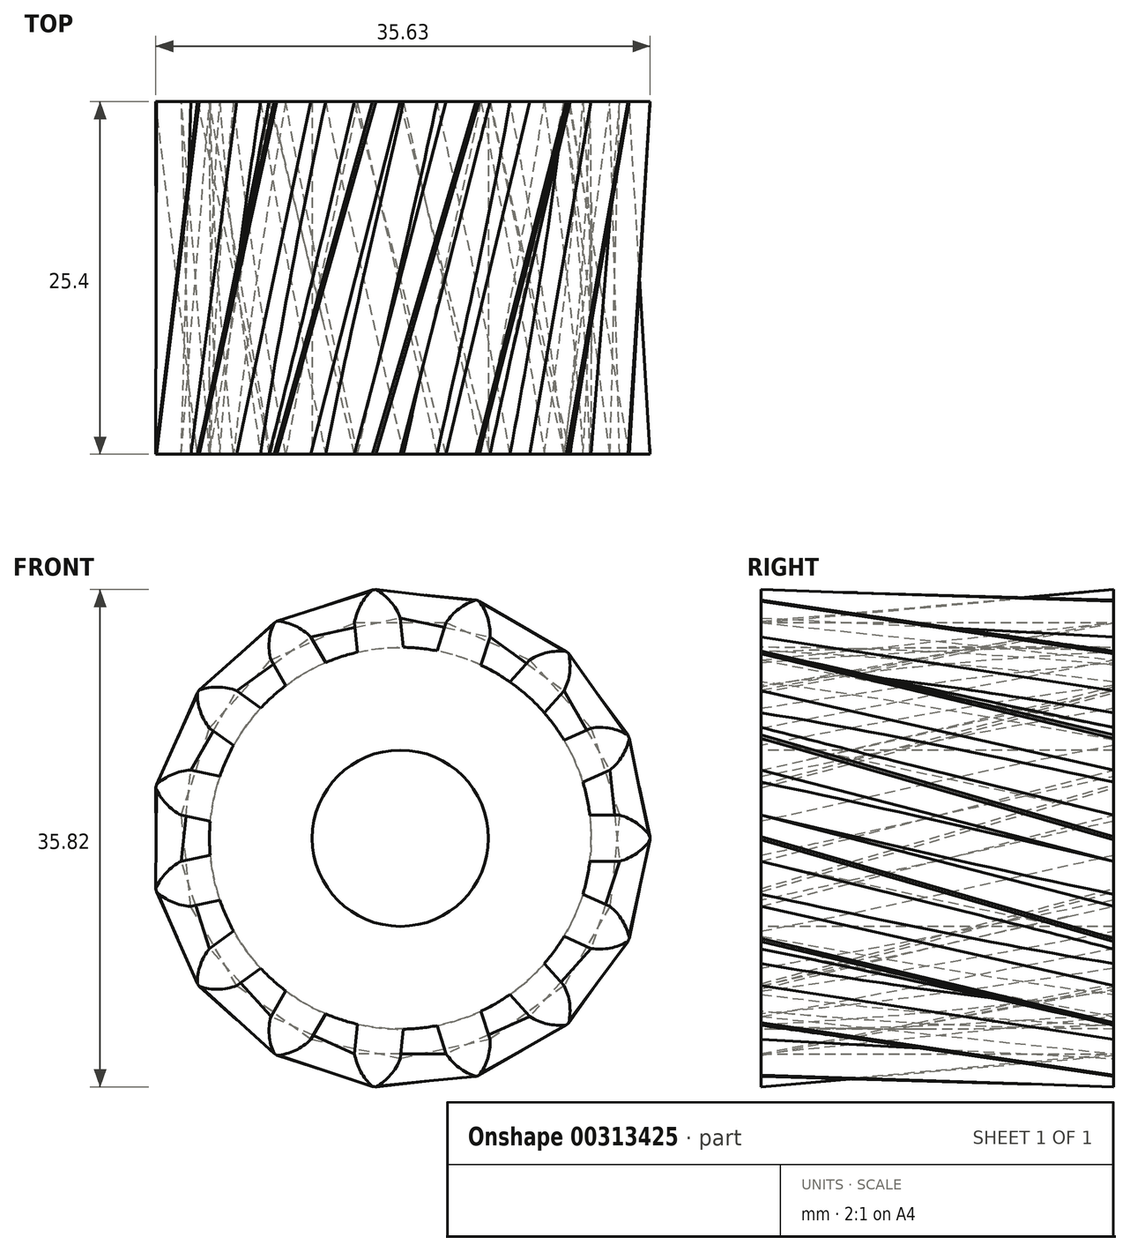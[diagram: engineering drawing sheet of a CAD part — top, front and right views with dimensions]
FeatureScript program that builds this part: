
annotation { "Feature Type Name" : "Feature", "Feature Type Description" : "" }
export const myFeature = defineFeature(function(context is Context, id is Id, definition is map)
    precondition{}
    {
        {
            var Q0;
            Q0=qCreatedBy(makeId("Front.planeOp"),FACE);
            var sketch = newSketch(context, id + "F0", { "sketchPlane" : qUnion([Q0])});
            skCircle(sketch, "E0", {"center": v(0, 0) * mm, "radius": 13.75 * mm});
            skArc(sketch, "E1.trimOffspring", {"start": v(0, 15.88) * mm, "mid": v(-0.7, 17.05) * mm, "end": v(-1.76, 17.9) * mm});
            skLineSegment(sketch, "E2", {"start": v(0, 15.88) * mm, "end": v(0.22, 13.75) * mm});
            skLineSegment(sketch, "E3", {"start": v(-1.76, 17.9) * mm, "end": v(-1.88, 17.9) * mm});
            skLineSegment(sketch, "E4.MirrorCS", {"start": v(-3.3, 15.53) * mm, "end": v(-3.08, 13.4) * mm});
            skArc(sketch, "E5.MirrorCS", {"start": v(-3.3, 15.53) * mm, "mid": v(-2.86, 16.82) * mm, "end": v(-2, 17.88) * mm});
            skLineSegment(sketch, "E6.MirrorCS", {"start": v(-2, 17.88) * mm, "end": v(-1.88, 17.9) * mm});
            skLineSegment(sketch, "E7.1.0", {"start": v(-6.46, 14.5) * mm, "end": v(-5.39, 12.65) * mm});
            skArc(sketch, "E7.1.1", {"start": v(-6.46, 14.5) * mm, "mid": v(-7.57, 15.29) * mm, "end": v(-8.9, 15.65) * mm});
            skLineSegment(sketch, "E7.1.2", {"start": v(-8.9, 15.65) * mm, "end": v(-9, 15.59) * mm});
            skLineSegment(sketch, "E7.1.3", {"start": v(-9.1, 15.52) * mm, "end": v(-9, 15.59) * mm});
            skArc(sketch, "E7.1.4", {"start": v(-9.33, 12.84) * mm, "mid": v(-9.45, 14.2) * mm, "end": v(-9.1, 15.52) * mm});
            skLineSegment(sketch, "E7.1.5", {"start": v(-9.33, 12.84) * mm, "end": v(-8.26, 11) * mm});
            skLineSegment(sketch, "E7.2.0", {"start": v(-11.8, 10.62) * mm, "end": v(-10.07, 9.37) * mm});
            skArc(sketch, "E7.2.1", {"start": v(-11.8, 10.62) * mm, "mid": v(-13.14, 10.88) * mm, "end": v(-14.49, 10.68) * mm});
            skLineSegment(sketch, "E7.2.2", {"start": v(-14.49, 10.68) * mm, "end": v(-14.56, 10.58) * mm});
            skLineSegment(sketch, "E7.2.3", {"start": v(-14.63, 10.48) * mm, "end": v(-14.56, 10.58) * mm});
            skArc(sketch, "E7.2.4", {"start": v(-13.75, 7.94) * mm, "mid": v(-14.41, 9.13) * mm, "end": v(-14.63, 10.48) * mm});
            skLineSegment(sketch, "E7.2.5", {"start": v(-13.75, 7.94) * mm, "end": v(-12.02, 6.68) * mm});
            skLineSegment(sketch, "E7.3.0", {"start": v(-15.1, 4.9) * mm, "end": v(-13.01, 4.46) * mm});
            skArc(sketch, "E7.3.1", {"start": v(-15.1, 4.9) * mm, "mid": v(-16.43, 4.6) * mm, "end": v(-17.58, 3.86) * mm});
            skLineSegment(sketch, "E7.3.2", {"start": v(-17.58, 3.86) * mm, "end": v(-17.6, 3.74) * mm});
            skLineSegment(sketch, "E7.3.3", {"start": v(-17.63, 3.62) * mm, "end": v(-17.6, 3.74) * mm});
            skArc(sketch, "E7.3.4", {"start": v(-15.79, 1.66) * mm, "mid": v(-16.88, 2.48) * mm, "end": v(-17.63, 3.62) * mm});
            skLineSegment(sketch, "E7.3.5", {"start": v(-15.79, 1.66) * mm, "end": v(-13.7, 1.22) * mm});
            skLineSegment(sketch, "E7.4.0", {"start": v(-15.79, -1.66) * mm, "end": v(-13.7, -1.22) * mm});
            skArc(sketch, "E7.4.1", {"start": v(-15.79, -1.66) * mm, "mid": v(-16.88, -2.48) * mm, "end": v(-17.63, -3.62) * mm});
            skLineSegment(sketch, "E7.4.2", {"start": v(-17.63, -3.62) * mm, "end": v(-17.6, -3.74) * mm});
            skLineSegment(sketch, "E7.4.3", {"start": v(-17.58, -3.86) * mm, "end": v(-17.6, -3.74) * mm});
            skArc(sketch, "E7.4.4", {"start": v(-15.1, -4.9) * mm, "mid": v(-16.43, -4.6) * mm, "end": v(-17.58, -3.86) * mm});
            skLineSegment(sketch, "E7.4.5", {"start": v(-15.1, -4.9) * mm, "end": v(-13.01, -4.46) * mm});
            skLineSegment(sketch, "E7.5.0", {"start": v(-13.75, -7.94) * mm, "end": v(-12.02, -6.68) * mm});
            skArc(sketch, "E7.5.1", {"start": v(-13.75, -7.94) * mm, "mid": v(-14.41, -9.13) * mm, "end": v(-14.63, -10.48) * mm});
            skLineSegment(sketch, "E7.5.2", {"start": v(-14.63, -10.48) * mm, "end": v(-14.56, -10.58) * mm});
            skLineSegment(sketch, "E7.5.3", {"start": v(-14.49, -10.68) * mm, "end": v(-14.56, -10.58) * mm});
            skArc(sketch, "E7.5.4", {"start": v(-11.8, -10.62) * mm, "mid": v(-13.14, -10.88) * mm, "end": v(-14.49, -10.68) * mm});
            skLineSegment(sketch, "E7.5.5", {"start": v(-11.8, -10.62) * mm, "end": v(-10.07, -9.37) * mm});
            skLineSegment(sketch, "E7.6.0", {"start": v(-9.33, -12.84) * mm, "end": v(-8.26, -11) * mm});
            skArc(sketch, "E7.6.1", {"start": v(-9.33, -12.84) * mm, "mid": v(-9.45, -14.2) * mm, "end": v(-9.1, -15.52) * mm});
            skLineSegment(sketch, "E7.6.2", {"start": v(-9.1, -15.52) * mm, "end": v(-9, -15.59) * mm});
            skLineSegment(sketch, "E7.6.3", {"start": v(-8.9, -15.65) * mm, "end": v(-9, -15.59) * mm});
            skArc(sketch, "E7.6.4", {"start": v(-6.46, -14.5) * mm, "mid": v(-7.57, -15.29) * mm, "end": v(-8.9, -15.65) * mm});
            skLineSegment(sketch, "E7.6.5", {"start": v(-6.46, -14.5) * mm, "end": v(-5.39, -12.65) * mm});
            skLineSegment(sketch, "E7.7.0", {"start": v(-3.3, -15.53) * mm, "end": v(-3.08, -13.4) * mm});
            skArc(sketch, "E7.7.1", {"start": v(-3.3, -15.53) * mm, "mid": v(-2.86, -16.82) * mm, "end": v(-2, -17.88) * mm});
            skLineSegment(sketch, "E7.7.2", {"start": v(-2, -17.88) * mm, "end": v(-1.88, -17.9) * mm});
            skLineSegment(sketch, "E7.7.3", {"start": v(-1.76, -17.9) * mm, "end": v(-1.88, -17.9) * mm});
            skArc(sketch, "E7.7.4", {"start": v(0, -15.88) * mm, "mid": v(-0.7, -17.05) * mm, "end": v(-1.76, -17.9) * mm});
            skLineSegment(sketch, "E7.7.5", {"start": v(0, -15.88) * mm, "end": v(0.22, -13.75) * mm});
            skLineSegment(sketch, "E7.8.0", {"start": v(3.3, -15.53) * mm, "end": v(2.64, -13.5) * mm});
            skArc(sketch, "E7.8.1", {"start": v(3.3, -15.53) * mm, "mid": v(4.23, -16.53) * mm, "end": v(5.44, -17.15) * mm});
            skLineSegment(sketch, "E7.8.2", {"start": v(5.44, -17.15) * mm, "end": v(5.56, -17.12) * mm});
            skLineSegment(sketch, "E7.8.3", {"start": v(5.68, -17.08) * mm, "end": v(5.56, -17.12) * mm});
            skArc(sketch, "E7.8.4", {"start": v(6.46, -14.5) * mm, "mid": v(6.3, -15.86) * mm, "end": v(5.68, -17.08) * mm});
            skLineSegment(sketch, "E7.8.5", {"start": v(6.46, -14.5) * mm, "end": v(5.8, -12.47) * mm});
            skLineSegment(sketch, "E7.9.0", {"start": v(9.33, -12.84) * mm, "end": v(7.9, -11.26) * mm});
            skArc(sketch, "E7.9.1", {"start": v(9.33, -12.84) * mm, "mid": v(10.59, -13.38) * mm, "end": v(11.95, -13.46) * mm});
            skLineSegment(sketch, "E7.9.2", {"start": v(11.95, -13.46) * mm, "end": v(12.04, -13.37) * mm});
            skLineSegment(sketch, "E7.9.3", {"start": v(12.13, -13.3) * mm, "end": v(12.04, -13.37) * mm});
            skArc(sketch, "E7.9.4", {"start": v(11.8, -10.62) * mm, "mid": v(12.2, -11.93) * mm, "end": v(12.13, -13.3) * mm});
            skLineSegment(sketch, "E7.9.5", {"start": v(11.8, -10.62) * mm, "end": v(10.37, -9.04) * mm});
            skLineSegment(sketch, "E7.10.0", {"start": v(13.75, -7.94) * mm, "end": v(11.8, -7.07) * mm});
            skArc(sketch, "E7.10.1", {"start": v(13.75, -7.94) * mm, "mid": v(15.11, -7.92) * mm, "end": v(16.39, -7.43) * mm});
            skLineSegment(sketch, "E7.10.2", {"start": v(16.39, -7.43) * mm, "end": v(16.44, -7.32) * mm});
            skLineSegment(sketch, "E7.10.3", {"start": v(16.49, -7.2) * mm, "end": v(16.44, -7.32) * mm});
            skArc(sketch, "E7.10.4", {"start": v(15.1, -4.9) * mm, "mid": v(16, -5.94) * mm, "end": v(16.49, -7.2) * mm});
            skLineSegment(sketch, "E7.10.5", {"start": v(15.1, -4.9) * mm, "end": v(13.15, -4.04) * mm});
            skLineSegment(sketch, "E7.11.0", {"start": v(15.79, -1.66) * mm, "end": v(13.65, -1.66) * mm});
            skArc(sketch, "E7.11.1", {"start": v(15.79, -1.66) * mm, "mid": v(17.03, -1.08) * mm, "end": v(18, -0.12) * mm});
            skLineSegment(sketch, "E7.11.2", {"start": v(18, -0.12) * mm, "end": v(18, 0) * mm});
            skLineSegment(sketch, "E7.11.3", {"start": v(18, 0.12) * mm, "end": v(18, 0) * mm});
            skArc(sketch, "E7.11.4", {"start": v(15.79, 1.66) * mm, "mid": v(17.03, 1.08) * mm, "end": v(18, 0.12) * mm});
            skLineSegment(sketch, "E7.11.5", {"start": v(15.79, 1.66) * mm, "end": v(13.65, 1.66) * mm});
            skLineSegment(sketch, "E7.12.0", {"start": v(15.1, 4.9) * mm, "end": v(13.15, 4.04) * mm});
            skArc(sketch, "E7.12.1", {"start": v(15.1, 4.9) * mm, "mid": v(16, 5.94) * mm, "end": v(16.49, 7.2) * mm});
            skLineSegment(sketch, "E7.12.2", {"start": v(16.49, 7.2) * mm, "end": v(16.44, 7.32) * mm});
            skLineSegment(sketch, "E7.12.3", {"start": v(16.39, 7.43) * mm, "end": v(16.44, 7.32) * mm});
            skArc(sketch, "E7.12.4", {"start": v(13.75, 7.94) * mm, "mid": v(15.11, 7.92) * mm, "end": v(16.39, 7.43) * mm});
            skLineSegment(sketch, "E7.12.5", {"start": v(13.75, 7.94) * mm, "end": v(11.8, 7.07) * mm});
            skLineSegment(sketch, "E7.13.0", {"start": v(11.8, 10.62) * mm, "end": v(10.37, 9.04) * mm});
            skArc(sketch, "E7.13.1", {"start": v(11.8, 10.62) * mm, "mid": v(12.2, 11.93) * mm, "end": v(12.13, 13.3) * mm});
            skLineSegment(sketch, "E7.13.2", {"start": v(12.13, 13.3) * mm, "end": v(12.04, 13.37) * mm});
            skLineSegment(sketch, "E7.13.3", {"start": v(11.95, 13.46) * mm, "end": v(12.04, 13.37) * mm});
            skArc(sketch, "E7.13.4", {"start": v(9.33, 12.84) * mm, "mid": v(10.59, 13.38) * mm, "end": v(11.95, 13.46) * mm});
            skLineSegment(sketch, "E7.13.5", {"start": v(9.33, 12.84) * mm, "end": v(7.9, 11.26) * mm});
            skLineSegment(sketch, "E7.14.0", {"start": v(6.46, 14.5) * mm, "end": v(5.8, 12.47) * mm});
            skArc(sketch, "E7.14.1", {"start": v(6.46, 14.5) * mm, "mid": v(6.3, 15.86) * mm, "end": v(5.68, 17.08) * mm});
            skLineSegment(sketch, "E7.14.2", {"start": v(5.68, 17.08) * mm, "end": v(5.56, 17.12) * mm});
            skLineSegment(sketch, "E7.14.3", {"start": v(5.44, 17.15) * mm, "end": v(5.56, 17.12) * mm});
            skArc(sketch, "E7.14.4", {"start": v(3.3, 15.53) * mm, "mid": v(4.23, 16.53) * mm, "end": v(5.44, 17.15) * mm});
            skLineSegment(sketch, "E7.14.5", {"start": v(3.3, 15.53) * mm, "end": v(2.64, 13.5) * mm});
            skSolve(sketch);
        }
        {
            var Q0;
            Q0=qCreatedBy(makeId("Front.planeOp"),FACE);
            cPlane(context, id + "F1", {"entities" : qUnion([Q0]), "cplaneType" : CPlaneType.OFFSET, "offset" : 25.4 * mm, "width" : 152.4 * mm, "height" : 152.4 * mm});
        }
        {
            var Q0;
            Q0=qCreatedBy(id+"F1.planeOp",FACE);
            var sketch = newSketch(context, id + "F2", { "sketchPlane" : qUnion([Q0])});
            skCircle(sketch, "E8", {"center": v(0, 0) * mm, "radius": 13.75 * mm});
            skArc(sketch, "E9.trimOffspring", {"start": v(0, 15.88) * mm, "mid": v(-0.7, 17.05) * mm, "end": v(-1.76, 17.9) * mm});
            skLineSegment(sketch, "E10", {"start": v(0, 15.88) * mm, "end": v(0.22, 13.75) * mm});
            skLineSegment(sketch, "E11", {"start": v(-1.76, 17.9) * mm, "end": v(-1.88, 17.9) * mm});
            skLineSegment(sketch, "E12.MirrorCS", {"start": v(-3.3, 15.53) * mm, "end": v(-3.08, 13.4) * mm});
            skArc(sketch, "E13.MirrorCS", {"start": v(-3.3, 15.53) * mm, "mid": v(-2.86, 16.82) * mm, "end": v(-2, 17.88) * mm});
            skLineSegment(sketch, "E14.MirrorCS", {"start": v(-2, 17.88) * mm, "end": v(-1.88, 17.9) * mm});
            skLineSegment(sketch, "E15.1.0", {"start": v(-6.46, 14.5) * mm, "end": v(-5.39, 12.65) * mm});
            skArc(sketch, "E15.1.1", {"start": v(-6.46, 14.5) * mm, "mid": v(-7.57, 15.29) * mm, "end": v(-8.9, 15.65) * mm});
            skLineSegment(sketch, "E15.1.2", {"start": v(-8.9, 15.65) * mm, "end": v(-9, 15.59) * mm});
            skLineSegment(sketch, "E15.1.3", {"start": v(-9.1, 15.52) * mm, "end": v(-9, 15.59) * mm});
            skArc(sketch, "E15.1.4", {"start": v(-9.33, 12.84) * mm, "mid": v(-9.45, 14.2) * mm, "end": v(-9.1, 15.52) * mm});
            skLineSegment(sketch, "E15.1.5", {"start": v(-9.33, 12.84) * mm, "end": v(-8.26, 11) * mm});
            skLineSegment(sketch, "E15.2.0", {"start": v(-11.8, 10.62) * mm, "end": v(-10.07, 9.37) * mm});
            skArc(sketch, "E15.2.1", {"start": v(-11.8, 10.62) * mm, "mid": v(-13.14, 10.88) * mm, "end": v(-14.49, 10.68) * mm});
            skLineSegment(sketch, "E15.2.2", {"start": v(-14.49, 10.68) * mm, "end": v(-14.56, 10.58) * mm});
            skLineSegment(sketch, "E15.2.3", {"start": v(-14.63, 10.48) * mm, "end": v(-14.56, 10.58) * mm});
            skArc(sketch, "E15.2.4", {"start": v(-13.75, 7.94) * mm, "mid": v(-14.41, 9.13) * mm, "end": v(-14.63, 10.48) * mm});
            skLineSegment(sketch, "E15.2.5", {"start": v(-13.75, 7.94) * mm, "end": v(-12.02, 6.68) * mm});
            skLineSegment(sketch, "E15.3.0", {"start": v(-15.1, 4.9) * mm, "end": v(-13.01, 4.46) * mm});
            skArc(sketch, "E15.3.1", {"start": v(-15.1, 4.9) * mm, "mid": v(-16.43, 4.6) * mm, "end": v(-17.58, 3.86) * mm});
            skLineSegment(sketch, "E15.3.2", {"start": v(-17.58, 3.86) * mm, "end": v(-17.6, 3.74) * mm});
            skLineSegment(sketch, "E15.3.3", {"start": v(-17.63, 3.62) * mm, "end": v(-17.6, 3.74) * mm});
            skArc(sketch, "E15.3.4", {"start": v(-15.79, 1.66) * mm, "mid": v(-16.88, 2.48) * mm, "end": v(-17.63, 3.62) * mm});
            skLineSegment(sketch, "E15.3.5", {"start": v(-15.79, 1.66) * mm, "end": v(-13.7, 1.22) * mm});
            skLineSegment(sketch, "E15.4.0", {"start": v(-15.79, -1.66) * mm, "end": v(-13.7, -1.22) * mm});
            skArc(sketch, "E15.4.1", {"start": v(-15.79, -1.66) * mm, "mid": v(-16.88, -2.48) * mm, "end": v(-17.63, -3.62) * mm});
            skLineSegment(sketch, "E15.4.2", {"start": v(-17.63, -3.62) * mm, "end": v(-17.6, -3.74) * mm});
            skLineSegment(sketch, "E15.4.3", {"start": v(-17.58, -3.86) * mm, "end": v(-17.6, -3.74) * mm});
            skArc(sketch, "E15.4.4", {"start": v(-15.1, -4.9) * mm, "mid": v(-16.43, -4.6) * mm, "end": v(-17.58, -3.86) * mm});
            skLineSegment(sketch, "E15.4.5", {"start": v(-15.1, -4.9) * mm, "end": v(-13.01, -4.46) * mm});
            skLineSegment(sketch, "E15.5.0", {"start": v(-13.75, -7.94) * mm, "end": v(-12.02, -6.68) * mm});
            skArc(sketch, "E15.5.1", {"start": v(-13.75, -7.94) * mm, "mid": v(-14.41, -9.13) * mm, "end": v(-14.63, -10.48) * mm});
            skLineSegment(sketch, "E15.5.2", {"start": v(-14.63, -10.48) * mm, "end": v(-14.56, -10.58) * mm});
            skLineSegment(sketch, "E15.5.3", {"start": v(-14.49, -10.68) * mm, "end": v(-14.56, -10.58) * mm});
            skArc(sketch, "E15.5.4", {"start": v(-11.8, -10.62) * mm, "mid": v(-13.14, -10.88) * mm, "end": v(-14.49, -10.68) * mm});
            skLineSegment(sketch, "E15.5.5", {"start": v(-11.8, -10.62) * mm, "end": v(-10.07, -9.37) * mm});
            skLineSegment(sketch, "E15.6.0", {"start": v(-9.33, -12.84) * mm, "end": v(-8.26, -11) * mm});
            skArc(sketch, "E15.6.1", {"start": v(-9.33, -12.84) * mm, "mid": v(-9.45, -14.2) * mm, "end": v(-9.1, -15.52) * mm});
            skLineSegment(sketch, "E15.6.2", {"start": v(-9.1, -15.52) * mm, "end": v(-9, -15.59) * mm});
            skLineSegment(sketch, "E15.6.3", {"start": v(-8.9, -15.65) * mm, "end": v(-9, -15.59) * mm});
            skArc(sketch, "E15.6.4", {"start": v(-6.46, -14.5) * mm, "mid": v(-7.57, -15.29) * mm, "end": v(-8.9, -15.65) * mm});
            skLineSegment(sketch, "E15.6.5", {"start": v(-6.46, -14.5) * mm, "end": v(-5.39, -12.65) * mm});
            skLineSegment(sketch, "E15.7.0", {"start": v(-3.3, -15.53) * mm, "end": v(-3.08, -13.4) * mm});
            skArc(sketch, "E15.7.1", {"start": v(-3.3, -15.53) * mm, "mid": v(-2.86, -16.82) * mm, "end": v(-2, -17.88) * mm});
            skLineSegment(sketch, "E15.7.2", {"start": v(-2, -17.88) * mm, "end": v(-1.88, -17.9) * mm});
            skLineSegment(sketch, "E15.7.3", {"start": v(-1.76, -17.9) * mm, "end": v(-1.88, -17.9) * mm});
            skArc(sketch, "E15.7.4", {"start": v(0, -15.88) * mm, "mid": v(-0.7, -17.05) * mm, "end": v(-1.76, -17.9) * mm});
            skLineSegment(sketch, "E15.7.5", {"start": v(0, -15.88) * mm, "end": v(0.22, -13.75) * mm});
            skLineSegment(sketch, "E15.8.0", {"start": v(3.3, -15.53) * mm, "end": v(2.64, -13.5) * mm});
            skArc(sketch, "E15.8.1", {"start": v(3.3, -15.53) * mm, "mid": v(4.23, -16.53) * mm, "end": v(5.44, -17.15) * mm});
            skLineSegment(sketch, "E15.8.2", {"start": v(5.44, -17.15) * mm, "end": v(5.56, -17.12) * mm});
            skLineSegment(sketch, "E15.8.3", {"start": v(5.68, -17.08) * mm, "end": v(5.56, -17.12) * mm});
            skArc(sketch, "E15.8.4", {"start": v(6.46, -14.5) * mm, "mid": v(6.3, -15.86) * mm, "end": v(5.68, -17.08) * mm});
            skLineSegment(sketch, "E15.8.5", {"start": v(6.46, -14.5) * mm, "end": v(5.8, -12.47) * mm});
            skLineSegment(sketch, "E15.9.0", {"start": v(9.33, -12.84) * mm, "end": v(7.9, -11.26) * mm});
            skArc(sketch, "E15.9.1", {"start": v(9.33, -12.84) * mm, "mid": v(10.59, -13.38) * mm, "end": v(11.95, -13.46) * mm});
            skLineSegment(sketch, "E15.9.2", {"start": v(11.95, -13.46) * mm, "end": v(12.04, -13.37) * mm});
            skLineSegment(sketch, "E15.9.3", {"start": v(12.13, -13.3) * mm, "end": v(12.04, -13.37) * mm});
            skArc(sketch, "E15.9.4", {"start": v(11.8, -10.62) * mm, "mid": v(12.2, -11.93) * mm, "end": v(12.13, -13.3) * mm});
            skLineSegment(sketch, "E15.9.5", {"start": v(11.8, -10.62) * mm, "end": v(10.37, -9.04) * mm});
            skLineSegment(sketch, "E15.10.0", {"start": v(13.75, -7.94) * mm, "end": v(11.8, -7.07) * mm});
            skArc(sketch, "E15.10.1", {"start": v(13.75, -7.94) * mm, "mid": v(15.11, -7.92) * mm, "end": v(16.39, -7.43) * mm});
            skLineSegment(sketch, "E15.10.2", {"start": v(16.39, -7.43) * mm, "end": v(16.44, -7.32) * mm});
            skLineSegment(sketch, "E15.10.3", {"start": v(16.49, -7.2) * mm, "end": v(16.44, -7.32) * mm});
            skArc(sketch, "E15.10.4", {"start": v(15.1, -4.9) * mm, "mid": v(16, -5.94) * mm, "end": v(16.49, -7.2) * mm});
            skLineSegment(sketch, "E15.10.5", {"start": v(15.1, -4.9) * mm, "end": v(13.15, -4.04) * mm});
            skLineSegment(sketch, "E15.11.0", {"start": v(15.79, -1.66) * mm, "end": v(13.65, -1.66) * mm});
            skArc(sketch, "E15.11.1", {"start": v(15.79, -1.66) * mm, "mid": v(17.03, -1.08) * mm, "end": v(18, -0.12) * mm});
            skLineSegment(sketch, "E15.11.2", {"start": v(18, -0.12) * mm, "end": v(18, 0) * mm});
            skLineSegment(sketch, "E15.11.3", {"start": v(18, 0.12) * mm, "end": v(18, 0) * mm});
            skArc(sketch, "E15.11.4", {"start": v(15.79, 1.66) * mm, "mid": v(17.03, 1.08) * mm, "end": v(18, 0.12) * mm});
            skLineSegment(sketch, "E15.11.5", {"start": v(15.79, 1.66) * mm, "end": v(13.65, 1.66) * mm});
            skLineSegment(sketch, "E15.12.0", {"start": v(15.1, 4.9) * mm, "end": v(13.15, 4.04) * mm});
            skArc(sketch, "E15.12.1", {"start": v(15.1, 4.9) * mm, "mid": v(16, 5.94) * mm, "end": v(16.49, 7.2) * mm});
            skLineSegment(sketch, "E15.12.2", {"start": v(16.49, 7.2) * mm, "end": v(16.44, 7.32) * mm});
            skLineSegment(sketch, "E15.12.3", {"start": v(16.39, 7.43) * mm, "end": v(16.44, 7.32) * mm});
            skArc(sketch, "E15.12.4", {"start": v(13.75, 7.94) * mm, "mid": v(15.11, 7.92) * mm, "end": v(16.39, 7.43) * mm});
            skLineSegment(sketch, "E15.12.5", {"start": v(13.75, 7.94) * mm, "end": v(11.8, 7.07) * mm});
            skLineSegment(sketch, "E15.13.0", {"start": v(11.8, 10.62) * mm, "end": v(10.37, 9.04) * mm});
            skArc(sketch, "E15.13.1", {"start": v(11.8, 10.62) * mm, "mid": v(12.2, 11.93) * mm, "end": v(12.13, 13.3) * mm});
            skLineSegment(sketch, "E15.13.2", {"start": v(12.13, 13.3) * mm, "end": v(12.04, 13.37) * mm});
            skLineSegment(sketch, "E15.13.3", {"start": v(11.95, 13.46) * mm, "end": v(12.04, 13.37) * mm});
            skArc(sketch, "E15.13.4", {"start": v(9.33, 12.84) * mm, "mid": v(10.59, 13.38) * mm, "end": v(11.95, 13.46) * mm});
            skLineSegment(sketch, "E15.13.5", {"start": v(9.33, 12.84) * mm, "end": v(7.9, 11.26) * mm});
            skLineSegment(sketch, "E15.14.0", {"start": v(6.46, 14.5) * mm, "end": v(5.8, 12.47) * mm});
            skArc(sketch, "E15.14.1", {"start": v(6.46, 14.5) * mm, "mid": v(6.3, 15.86) * mm, "end": v(5.68, 17.08) * mm});
            skLineSegment(sketch, "E15.14.2", {"start": v(5.68, 17.08) * mm, "end": v(5.56, 17.12) * mm});
            skLineSegment(sketch, "E15.14.3", {"start": v(5.44, 17.15) * mm, "end": v(5.56, 17.12) * mm});
            skArc(sketch, "E15.14.4", {"start": v(3.3, 15.53) * mm, "mid": v(4.23, 16.53) * mm, "end": v(5.44, 17.15) * mm});
            skLineSegment(sketch, "E15.14.5", {"start": v(3.3, 15.53) * mm, "end": v(2.64, 13.5) * mm});
            skSolve(sketch);
        }
        {
            var Q0;
            Q0=makeQuery(id+"F2.imprint","IMPRINT",FACE,{"disambiguationData":[TD([[makeQuery(id+"F2.imprint","IMPRINT",EDGE,{"derivedFrom":sQuery(id+"F2.wireOp",EDGE,"E9.trimOffspring")}),1.0]])]});
            var Q1;
            {var subQ0=sQuery(id+"F0.wireOp",EDGE,"E7.14.0");Q1=makeQuery(id+"F0.imprint","IMPRINT",FACE,{"disambiguationData":[TD([[makeQuery(id+"F0.imprint","IMPRINT",EDGE,{"derivedFrom":subQ0}),-1.0]])]});}
            loft(context, id + "F3", {"sheetProfilesArray" : [{ "sheetProfileEntities" : qUnion([Q0]) }, { "sheetProfileEntities" : qUnion([Q1]) }]});
        }
        {
            var Q1;
            {var subQ0=sQuery(id+"F2.wireOp",EDGE,"E8");var subQ18=makeQuery(id+"F2.imprint","INTERSECT",VERTEX,{"derivedFrom":[subQ0,sQuery(id+"F2.wireOp",EDGE,"E15.11.5")]});Q1=makeQuery(id+"F2.imprint","IMPRINT",FACE,{"disambiguationData":[TD([[makeQuery(id+"F2.imprint","IMPRINT",EDGE,{"disambiguationData":[TD([[subQ18,-1.0]])],"derivedFrom":subQ0}),1.0]])]});}
            var Q2;
            {var subQ0=sQuery(id+"F0.wireOp",EDGE,"E0");var subQ18=makeQuery(id+"F0.imprint","INTERSECT",VERTEX,{"derivedFrom":[subQ0,sQuery(id+"F0.wireOp",EDGE,"E7.11.5")]});Q2=makeQuery(id+"F0.imprint","IMPRINT",FACE,{"disambiguationData":[TD([[makeQuery(id+"F0.imprint","IMPRINT",EDGE,{"disambiguationData":[TD([[subQ18,-1.0]])],"derivedFrom":subQ0}),1.0]])]});}
            loft(context, id + "F4", {"operationType" : NewBodyOperationType.ADD, "sheetProfilesArray" : [{ "sheetProfileEntities" : qUnion([Q1]) }, { "sheetProfileEntities" : qUnion([Q2]) }]});
        }
        {
            var Q1;
            {var subQ0=sQuery(id+"F2.wireOp",EDGE,"E15.14.0");Q1=makeQuery(id+"F2.imprint","IMPRINT",FACE,{"disambiguationData":[TD([[makeQuery(id+"F2.imprint","IMPRINT",EDGE,{"derivedFrom":subQ0}),-1.0]])]});}
            var Q2;
            {var subQ0=sQuery(id+"F0.wireOp",EDGE,"E7.13.0");Q2=makeQuery(id+"F0.imprint","IMPRINT",FACE,{"disambiguationData":[TD([[makeQuery(id+"F0.imprint","IMPRINT",EDGE,{"derivedFrom":subQ0}),-1.0]])]});}
            loft(context, id + "F5", {"operationType" : NewBodyOperationType.ADD, "sheetProfilesArray" : [{ "sheetProfileEntities" : qUnion([Q1]) }, { "sheetProfileEntities" : qUnion([Q2]) }]});
        }
        {
            var Q1;
            {var subQ0=sQuery(id+"F2.wireOp",EDGE,"E15.1.0");Q1=makeQuery(id+"F2.imprint","IMPRINT",FACE,{"disambiguationData":[TD([[makeQuery(id+"F2.imprint","IMPRINT",EDGE,{"derivedFrom":subQ0}),-1.0]])]});}
            var Q2;
            Q2=makeQuery(id+"F0.imprint","IMPRINT",FACE,{"disambiguationData":[TD([[makeQuery(id+"F0.imprint","IMPRINT",EDGE,{"derivedFrom":sQuery(id+"F0.wireOp",EDGE,"E1.trimOffspring")}),1.0]])]});
            loft(context, id + "F6", {"operationType" : NewBodyOperationType.ADD, "sheetProfilesArray" : [{ "sheetProfileEntities" : qUnion([Q1]) }, { "sheetProfileEntities" : qUnion([Q2]) }]});
        }
        {
            var Q1;
            {var subQ0=sQuery(id+"F2.wireOp",EDGE,"E15.2.0");Q1=makeQuery(id+"F2.imprint","IMPRINT",FACE,{"disambiguationData":[TD([[makeQuery(id+"F2.imprint","IMPRINT",EDGE,{"derivedFrom":subQ0}),-1.0]])]});}
            var Q2;
            {var subQ0=sQuery(id+"F0.wireOp",EDGE,"E7.1.0");Q2=makeQuery(id+"F0.imprint","IMPRINT",FACE,{"disambiguationData":[TD([[makeQuery(id+"F0.imprint","IMPRINT",EDGE,{"derivedFrom":subQ0}),-1.0]])]});}
            loft(context, id + "F7", {"operationType" : NewBodyOperationType.ADD, "sheetProfilesArray" : [{ "sheetProfileEntities" : qUnion([Q1]) }, { "sheetProfileEntities" : qUnion([Q2]) }]});
        }
        {
            var Q1;
            {var subQ0=sQuery(id+"F2.wireOp",EDGE,"E15.13.0");Q1=makeQuery(id+"F2.imprint","IMPRINT",FACE,{"disambiguationData":[TD([[makeQuery(id+"F2.imprint","IMPRINT",EDGE,{"derivedFrom":subQ0}),-1.0]])]});}
            var Q2;
            {var subQ0=sQuery(id+"F0.wireOp",EDGE,"E7.12.0");Q2=makeQuery(id+"F0.imprint","IMPRINT",FACE,{"disambiguationData":[TD([[makeQuery(id+"F0.imprint","IMPRINT",EDGE,{"derivedFrom":subQ0}),-1.0]])]});}
            loft(context, id + "F8", {"operationType" : NewBodyOperationType.ADD, "sheetProfilesArray" : [{ "sheetProfileEntities" : qUnion([Q1]) }, { "sheetProfileEntities" : qUnion([Q2]) }]});
        }
        {
            var Q1;
            {var subQ0=sQuery(id+"F2.wireOp",EDGE,"E15.12.0");Q1=makeQuery(id+"F2.imprint","IMPRINT",FACE,{"disambiguationData":[TD([[makeQuery(id+"F2.imprint","IMPRINT",EDGE,{"derivedFrom":subQ0}),-1.0]])]});}
            var Q2;
            {var subQ0=sQuery(id+"F0.wireOp",EDGE,"E7.11.0");Q2=makeQuery(id+"F0.imprint","IMPRINT",FACE,{"disambiguationData":[TD([[makeQuery(id+"F0.imprint","IMPRINT",EDGE,{"derivedFrom":subQ0}),-1.0]])]});}
            loft(context, id + "F9", {"operationType" : NewBodyOperationType.ADD, "sheetProfilesArray" : [{ "sheetProfileEntities" : qUnion([Q1]) }, { "sheetProfileEntities" : qUnion([Q2]) }]});
        }
        {
            var Q1;
            {var subQ0=sQuery(id+"F2.wireOp",EDGE,"E15.11.0");Q1=makeQuery(id+"F2.imprint","IMPRINT",FACE,{"disambiguationData":[TD([[makeQuery(id+"F2.imprint","IMPRINT",EDGE,{"derivedFrom":subQ0}),-1.0]])]});}
            var Q2;
            {var subQ0=sQuery(id+"F0.wireOp",EDGE,"E7.10.0");Q2=makeQuery(id+"F0.imprint","IMPRINT",FACE,{"disambiguationData":[TD([[makeQuery(id+"F0.imprint","IMPRINT",EDGE,{"derivedFrom":subQ0}),-1.0]])]});}
            loft(context, id + "F10", {"operationType" : NewBodyOperationType.ADD, "sheetProfilesArray" : [{ "sheetProfileEntities" : qUnion([Q1]) }, { "sheetProfileEntities" : qUnion([Q2]) }]});
        }
        {
            var Q1;
            {var subQ0=sQuery(id+"F2.wireOp",EDGE,"E15.10.0");Q1=makeQuery(id+"F2.imprint","IMPRINT",FACE,{"disambiguationData":[TD([[makeQuery(id+"F2.imprint","IMPRINT",EDGE,{"derivedFrom":subQ0}),-1.0]])]});}
            var Q2;
            {var subQ0=sQuery(id+"F0.wireOp",EDGE,"E7.9.0");Q2=makeQuery(id+"F0.imprint","IMPRINT",FACE,{"disambiguationData":[TD([[makeQuery(id+"F0.imprint","IMPRINT",EDGE,{"derivedFrom":subQ0}),-1.0]])]});}
            loft(context, id + "F11", {"operationType" : NewBodyOperationType.ADD, "sheetProfilesArray" : [{ "sheetProfileEntities" : qUnion([Q1]) }, { "sheetProfileEntities" : qUnion([Q2]) }]});
        }
        {
            var Q1;
            {var subQ0=sQuery(id+"F2.wireOp",EDGE,"E15.9.0");Q1=makeQuery(id+"F2.imprint","IMPRINT",FACE,{"disambiguationData":[TD([[makeQuery(id+"F2.imprint","IMPRINT",EDGE,{"derivedFrom":subQ0}),-1.0]])]});}
            var Q2;
            {var subQ0=sQuery(id+"F0.wireOp",EDGE,"E7.8.0");Q2=makeQuery(id+"F0.imprint","IMPRINT",FACE,{"disambiguationData":[TD([[makeQuery(id+"F0.imprint","IMPRINT",EDGE,{"derivedFrom":subQ0}),-1.0]])]});}
            loft(context, id + "F12", {"operationType" : NewBodyOperationType.ADD, "sheetProfilesArray" : [{ "sheetProfileEntities" : qUnion([Q1]) }, { "sheetProfileEntities" : qUnion([Q2]) }]});
        }
        {
            var Q1;
            {var subQ0=sQuery(id+"F2.wireOp",EDGE,"E15.8.0");Q1=makeQuery(id+"F2.imprint","IMPRINT",FACE,{"disambiguationData":[TD([[makeQuery(id+"F2.imprint","IMPRINT",EDGE,{"derivedFrom":subQ0}),-1.0]])]});}
            var Q2;
            {var subQ0=sQuery(id+"F0.wireOp",EDGE,"E7.7.0");Q2=makeQuery(id+"F0.imprint","IMPRINT",FACE,{"disambiguationData":[TD([[makeQuery(id+"F0.imprint","IMPRINT",EDGE,{"derivedFrom":subQ0}),-1.0]])]});}
            loft(context, id + "F13", {"operationType" : NewBodyOperationType.ADD, "sheetProfilesArray" : [{ "sheetProfileEntities" : qUnion([Q1]) }, { "sheetProfileEntities" : qUnion([Q2]) }]});
        }
        {
            var Q1;
            {var subQ0=sQuery(id+"F2.wireOp",EDGE,"E15.3.0");Q1=makeQuery(id+"F2.imprint","IMPRINT",FACE,{"disambiguationData":[TD([[makeQuery(id+"F2.imprint","IMPRINT",EDGE,{"derivedFrom":subQ0}),-1.0]])]});}
            var Q2;
            {var subQ0=sQuery(id+"F0.wireOp",EDGE,"E7.2.0");Q2=makeQuery(id+"F0.imprint","IMPRINT",FACE,{"disambiguationData":[TD([[makeQuery(id+"F0.imprint","IMPRINT",EDGE,{"derivedFrom":subQ0}),-1.0]])]});}
            loft(context, id + "F14", {"operationType" : NewBodyOperationType.ADD, "sheetProfilesArray" : [{ "sheetProfileEntities" : qUnion([Q1]) }, { "sheetProfileEntities" : qUnion([Q2]) }]});
        }
        {
            var Q1;
            {var subQ0=sQuery(id+"F2.wireOp",EDGE,"E15.4.0");Q1=makeQuery(id+"F2.imprint","IMPRINT",FACE,{"disambiguationData":[TD([[makeQuery(id+"F2.imprint","IMPRINT",EDGE,{"derivedFrom":subQ0}),-1.0]])]});}
            var Q2;
            {var subQ0=sQuery(id+"F0.wireOp",EDGE,"E7.3.0");Q2=makeQuery(id+"F0.imprint","IMPRINT",FACE,{"disambiguationData":[TD([[makeQuery(id+"F0.imprint","IMPRINT",EDGE,{"derivedFrom":subQ0}),-1.0]])]});}
            loft(context, id + "F15", {"operationType" : NewBodyOperationType.ADD, "sheetProfilesArray" : [{ "sheetProfileEntities" : qUnion([Q1]) }, { "sheetProfileEntities" : qUnion([Q2]) }]});
        }
        {
            var Q1;
            {var subQ0=sQuery(id+"F2.wireOp",EDGE,"E15.5.0");Q1=makeQuery(id+"F2.imprint","IMPRINT",FACE,{"disambiguationData":[TD([[makeQuery(id+"F2.imprint","IMPRINT",EDGE,{"derivedFrom":subQ0}),-1.0]])]});}
            var Q2;
            {var subQ0=sQuery(id+"F0.wireOp",EDGE,"E7.4.0");Q2=makeQuery(id+"F0.imprint","IMPRINT",FACE,{"disambiguationData":[TD([[makeQuery(id+"F0.imprint","IMPRINT",EDGE,{"derivedFrom":subQ0}),-1.0]])]});}
            loft(context, id + "F16", {"operationType" : NewBodyOperationType.ADD, "sheetProfilesArray" : [{ "sheetProfileEntities" : qUnion([Q1]) }, { "sheetProfileEntities" : qUnion([Q2]) }]});
        }
        {
            var Q1;
            {var subQ0=sQuery(id+"F2.wireOp",EDGE,"E15.6.0");Q1=makeQuery(id+"F2.imprint","IMPRINT",FACE,{"disambiguationData":[TD([[makeQuery(id+"F2.imprint","IMPRINT",EDGE,{"derivedFrom":subQ0}),-1.0]])]});}
            var Q2;
            {var subQ0=sQuery(id+"F0.wireOp",EDGE,"E7.5.0");Q2=makeQuery(id+"F0.imprint","IMPRINT",FACE,{"disambiguationData":[TD([[makeQuery(id+"F0.imprint","IMPRINT",EDGE,{"derivedFrom":subQ0}),-1.0]])]});}
            loft(context, id + "F17", {"operationType" : NewBodyOperationType.ADD, "sheetProfilesArray" : [{ "sheetProfileEntities" : qUnion([Q1]) }, { "sheetProfileEntities" : qUnion([Q2]) }]});
        }
        {
            var Q1;
            {var subQ0=sQuery(id+"F2.wireOp",EDGE,"E15.7.0");Q1=makeQuery(id+"F2.imprint","IMPRINT",FACE,{"disambiguationData":[TD([[makeQuery(id+"F2.imprint","IMPRINT",EDGE,{"derivedFrom":subQ0}),-1.0]])]});}
            var Q2;
            {var subQ0=sQuery(id+"F0.wireOp",EDGE,"E7.6.0");Q2=makeQuery(id+"F0.imprint","IMPRINT",FACE,{"disambiguationData":[TD([[makeQuery(id+"F0.imprint","IMPRINT",EDGE,{"derivedFrom":subQ0}),-1.0]])]});}
            loft(context, id + "F18", {"operationType" : NewBodyOperationType.ADD, "sheetProfilesArray" : [{ "sheetProfileEntities" : qUnion([Q1]) }, { "sheetProfileEntities" : qUnion([Q2]) }]});
        }
        {
            var Q0;
            {var subQ0=sQuery(id+"F2.wireOp",EDGE,"E8");var subQ18=makeQuery(id+"F2.imprint","INTERSECT",VERTEX,{"derivedFrom":[subQ0,sQuery(id+"F2.wireOp",EDGE,"E15.11.5")]});Q0=makeQuery(id+"F2.imprint","IMPRINT",FACE,{"disambiguationData":[TD([[makeQuery(id+"F2.imprint","IMPRINT",EDGE,{"disambiguationData":[TD([[subQ18,-1.0]])],"derivedFrom":subQ0}),1.0]])]});}
            var sketch = newSketch(context, id + "F19", { "sketchPlane" : qUnion([Q0])});
            skCircle(sketch, "E16", {"center": v(0, 0) * mm, "radius": 6.35 * mm});
            skSolve(sketch);
        }
        {
            var Q0;
            Q0 = qSketchRegion(id + "F19", true);
            extrude(context, id + "F20", {"entities" : qUnion([Q0]), "operationType" : NewBodyOperationType.REMOVE, "oppositeDirection" : true, "depth" : 50.8 * mm});
        }
    });
